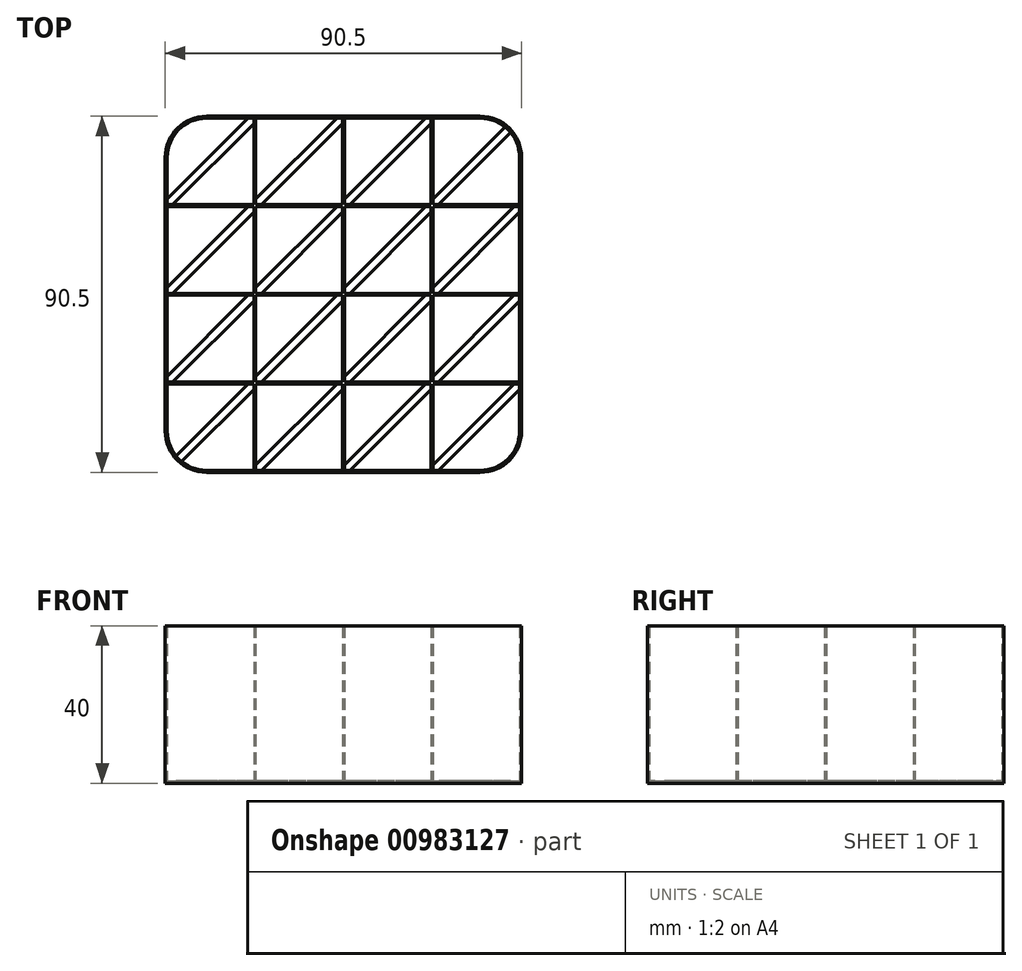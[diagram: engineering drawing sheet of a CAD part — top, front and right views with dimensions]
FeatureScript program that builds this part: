
annotation { "Feature Type Name" : "Feature", "Feature Type Description" : "" }
export const myFeature = defineFeature(function(context is Context, id is Id, definition is map)
    precondition{}
    {
        {
            assignVariable(context, id + "F0", {"name" : "wall", "anyValue" : 0.5});
        }
        {
            var Q0;
            Q0=qCreatedBy(makeId("Top.planeOp"),FACE);
            var sketch = newSketch(context, id + "F1", { "sketchPlane" : qUnion([Q0])});
            skLineSegment(sketch, "E0.bottom", {"start": v(0, 22) * mm, "end": v(22, 22) * mm});
            skLineSegment(sketch, "E0.top", {"start": v(0, 0) * mm, "end": v(22, 0) * mm});
            skLineSegment(sketch, "E0.left", {"start": v(0, 22) * mm, "end": v(0, 0) * mm});
            skLineSegment(sketch, "E0.right", {"start": v(22, 22) * mm, "end": v(22, 0) * mm});
            skLineSegment(sketch, "E1.0.1.0", {"start": v(22, 44.5) * mm, "end": v(22, 22.5) * mm});
            skLineSegment(sketch, "E1.0.1.1", {"start": v(0, 44.5) * mm, "end": v(22, 44.5) * mm});
            skLineSegment(sketch, "E1.0.1.2", {"start": v(0, 44.5) * mm, "end": v(0, 22.5) * mm});
            skLineSegment(sketch, "E1.0.1.3", {"start": v(0, 22.5) * mm, "end": v(22, 22.5) * mm});
            skLineSegment(sketch, "E1.0.2.0", {"start": v(22, 67) * mm, "end": v(22, 45) * mm});
            skLineSegment(sketch, "E1.0.2.1", {"start": v(0, 67) * mm, "end": v(22, 67) * mm});
            skLineSegment(sketch, "E1.0.2.2", {"start": v(0, 67) * mm, "end": v(0, 45) * mm});
            skLineSegment(sketch, "E1.0.2.3", {"start": v(0, 45) * mm, "end": v(22, 45) * mm});
            skLineSegment(sketch, "E1.0.3.0", {"start": v(22, 89.5) * mm, "end": v(22, 67.5) * mm});
            skLineSegment(sketch, "E1.0.3.1", {"start": v(0, 89.5) * mm, "end": v(22, 89.5) * mm});
            skLineSegment(sketch, "E1.0.3.2", {"start": v(0, 89.5) * mm, "end": v(0, 67.5) * mm});
            skLineSegment(sketch, "E1.0.3.3", {"start": v(0, 67.5) * mm, "end": v(22, 67.5) * mm});
            skLineSegment(sketch, "E1.1.0.0", {"start": v(44.5, 22) * mm, "end": v(44.5, 0) * mm});
            skLineSegment(sketch, "E1.1.0.1", {"start": v(22.5, 22) * mm, "end": v(44.5, 22) * mm});
            skLineSegment(sketch, "E1.1.0.2", {"start": v(22.5, 22) * mm, "end": v(22.5, 0) * mm});
            skLineSegment(sketch, "E1.1.0.3", {"start": v(22.5, 0) * mm, "end": v(44.5, 0) * mm});
            skLineSegment(sketch, "E1.1.1.0", {"start": v(44.5, 44.5) * mm, "end": v(44.5, 22.5) * mm});
            skLineSegment(sketch, "E1.1.1.1", {"start": v(22.5, 44.5) * mm, "end": v(44.5, 44.5) * mm});
            skLineSegment(sketch, "E1.1.1.2", {"start": v(22.5, 44.5) * mm, "end": v(22.5, 22.5) * mm});
            skLineSegment(sketch, "E1.1.1.3", {"start": v(22.5, 22.5) * mm, "end": v(44.5, 22.5) * mm});
            skLineSegment(sketch, "E1.1.2.0", {"start": v(44.5, 67) * mm, "end": v(44.5, 45) * mm});
            skLineSegment(sketch, "E1.1.2.1", {"start": v(22.5, 67) * mm, "end": v(44.5, 67) * mm});
            skLineSegment(sketch, "E1.1.2.2", {"start": v(22.5, 67) * mm, "end": v(22.5, 45) * mm});
            skLineSegment(sketch, "E1.1.2.3", {"start": v(22.5, 45) * mm, "end": v(44.5, 45) * mm});
            skLineSegment(sketch, "E1.1.3.0", {"start": v(44.5, 89.5) * mm, "end": v(44.5, 67.5) * mm});
            skLineSegment(sketch, "E1.1.3.1", {"start": v(22.5, 89.5) * mm, "end": v(44.5, 89.5) * mm});
            skLineSegment(sketch, "E1.1.3.2", {"start": v(22.5, 89.5) * mm, "end": v(22.5, 67.5) * mm});
            skLineSegment(sketch, "E1.1.3.3", {"start": v(22.5, 67.5) * mm, "end": v(44.5, 67.5) * mm});
            skLineSegment(sketch, "E1.2.0.0", {"start": v(67, 22) * mm, "end": v(67, 0) * mm});
            skLineSegment(sketch, "E1.2.0.1", {"start": v(45, 22) * mm, "end": v(67, 22) * mm});
            skLineSegment(sketch, "E1.2.0.2", {"start": v(45, 22) * mm, "end": v(45, 0) * mm});
            skLineSegment(sketch, "E1.2.0.3", {"start": v(45, 0) * mm, "end": v(67, 0) * mm});
            skLineSegment(sketch, "E1.2.1.0", {"start": v(67, 44.5) * mm, "end": v(67, 22.5) * mm});
            skLineSegment(sketch, "E1.2.1.1", {"start": v(45, 44.5) * mm, "end": v(67, 44.5) * mm});
            skLineSegment(sketch, "E1.2.1.2", {"start": v(45, 44.5) * mm, "end": v(45, 22.5) * mm});
            skLineSegment(sketch, "E1.2.1.3", {"start": v(45, 22.5) * mm, "end": v(67, 22.5) * mm});
            skLineSegment(sketch, "E1.2.2.0", {"start": v(67, 67) * mm, "end": v(67, 45) * mm});
            skLineSegment(sketch, "E1.2.2.1", {"start": v(45, 67) * mm, "end": v(67, 67) * mm});
            skLineSegment(sketch, "E1.2.2.2", {"start": v(45, 67) * mm, "end": v(45, 45) * mm});
            skLineSegment(sketch, "E1.2.2.3", {"start": v(45, 45) * mm, "end": v(67, 45) * mm});
            skLineSegment(sketch, "E1.2.3.0", {"start": v(67, 89.5) * mm, "end": v(67, 67.5) * mm});
            skLineSegment(sketch, "E1.2.3.1", {"start": v(45, 89.5) * mm, "end": v(67, 89.5) * mm});
            skLineSegment(sketch, "E1.2.3.2", {"start": v(45, 89.5) * mm, "end": v(45, 67.5) * mm});
            skLineSegment(sketch, "E1.2.3.3", {"start": v(45, 67.5) * mm, "end": v(67, 67.5) * mm});
            skLineSegment(sketch, "E1.3.0.0", {"start": v(89.5, 22) * mm, "end": v(89.5, 0) * mm});
            skLineSegment(sketch, "E1.3.0.1", {"start": v(67.5, 22) * mm, "end": v(89.5, 22) * mm});
            skLineSegment(sketch, "E1.3.0.2", {"start": v(67.5, 22) * mm, "end": v(67.5, 0) * mm});
            skLineSegment(sketch, "E1.3.0.3", {"start": v(67.5, 0) * mm, "end": v(89.5, 0) * mm});
            skLineSegment(sketch, "E1.3.1.0", {"start": v(89.5, 44.5) * mm, "end": v(89.5, 22.5) * mm});
            skLineSegment(sketch, "E1.3.1.1", {"start": v(67.5, 44.5) * mm, "end": v(89.5, 44.5) * mm});
            skLineSegment(sketch, "E1.3.1.2", {"start": v(67.5, 44.5) * mm, "end": v(67.5, 22.5) * mm});
            skLineSegment(sketch, "E1.3.1.3", {"start": v(67.5, 22.5) * mm, "end": v(89.5, 22.5) * mm});
            skLineSegment(sketch, "E1.3.2.0", {"start": v(89.5, 67) * mm, "end": v(89.5, 45) * mm});
            skLineSegment(sketch, "E1.3.2.1", {"start": v(67.5, 67) * mm, "end": v(89.5, 67) * mm});
            skLineSegment(sketch, "E1.3.2.2", {"start": v(67.5, 67) * mm, "end": v(67.5, 45) * mm});
            skLineSegment(sketch, "E1.3.2.3", {"start": v(67.5, 45) * mm, "end": v(89.5, 45) * mm});
            skLineSegment(sketch, "E1.3.3.0", {"start": v(89.5, 89.5) * mm, "end": v(89.5, 67.5) * mm});
            skLineSegment(sketch, "E1.3.3.1", {"start": v(67.5, 89.5) * mm, "end": v(89.5, 89.5) * mm});
            skLineSegment(sketch, "E1.3.3.2", {"start": v(67.5, 89.5) * mm, "end": v(67.5, 67.5) * mm});
            skLineSegment(sketch, "E1.3.3.3", {"start": v(67.5, 67.5) * mm, "end": v(89.5, 67.5) * mm});
            skLineSegment(sketch, "E1.direction1", {"start": v(22, 0) * mm, "end": v(44.5, 0) * mm, "construction": true});
            skLineSegment(sketch, "E1.direction2", {"start": v(22, 0) * mm, "end": v(22, 22.5) * mm, "construction": true});
            skLineSegment(sketch, "E2.bottom", {"start": v(-0.5, 90) * mm, "end": v(90, 90) * mm});
            skLineSegment(sketch, "E2.top", {"start": v(-0.5, -0.5) * mm, "end": v(90, -0.5) * mm});
            skLineSegment(sketch, "E2.left", {"start": v(-0.5, 90) * mm, "end": v(-0.5, -0.5) * mm});
            skLineSegment(sketch, "E2.right", {"start": v(90, 90) * mm, "end": v(90, -0.5) * mm});
            skSolve(sketch);
        }
        {
            var Q0;
            Q0=makeQuery(id+"F1.imprint","IMPRINT",FACE,{"disambiguationData":[TD([[makeQuery(id+"F1.imprint","IMPRINT",EDGE,{"derivedFrom":sQuery(id+"F1.wireOp",EDGE,"E0.bottom")}),1.0]])]});
            extrude(context, id + "F2", {"entities" : qUnion([Q0]), "depth" : 40 * mm, "offsetDistance" : 25 * mm});
        }
        {
            var Q0;
            Q0=makeQuery(id+"F2.opExtrude","CAP_FACE",FACE,{"disambiguationData":[OSD([sQuery(id+"F1.wireOp",EDGE,"E0.bottom"),sQuery(id+"F1.wireOp",EDGE,"E0.top"),sQuery(id+"F1.wireOp",EDGE,"E0.left"),sQuery(id+"F1.wireOp",EDGE,"E0.right"),sQuery(id+"F1.wireOp",EDGE,"E1.0.1.0"),sQuery(id+"F1.wireOp",EDGE,"E1.0.1.1"),sQuery(id+"F1.wireOp",EDGE,"E1.0.1.2"),sQuery(id+"F1.wireOp",EDGE,"E1.0.1.3"),sQuery(id+"F1.wireOp",EDGE,"E1.0.2.0"),sQuery(id+"F1.wireOp",EDGE,"E1.0.2.1"),sQuery(id+"F1.wireOp",EDGE,"E1.0.2.2"),sQuery(id+"F1.wireOp",EDGE,"E1.0.2.3"),sQuery(id+"F1.wireOp",EDGE,"E1.0.3.0"),sQuery(id+"F1.wireOp",EDGE,"E1.0.3.1"),sQuery(id+"F1.wireOp",EDGE,"E1.0.3.2"),sQuery(id+"F1.wireOp",EDGE,"E1.0.3.3"),sQuery(id+"F1.wireOp",EDGE,"E1.1.0.0"),sQuery(id+"F1.wireOp",EDGE,"E1.1.0.1"),sQuery(id+"F1.wireOp",EDGE,"E1.1.0.2"),sQuery(id+"F1.wireOp",EDGE,"E1.1.0.3"),sQuery(id+"F1.wireOp",EDGE,"E1.1.1.0"),sQuery(id+"F1.wireOp",EDGE,"E1.1.1.1"),sQuery(id+"F1.wireOp",EDGE,"E1.1.1.2"),sQuery(id+"F1.wireOp",EDGE,"E1.1.1.3"),sQuery(id+"F1.wireOp",EDGE,"E1.1.2.0"),sQuery(id+"F1.wireOp",EDGE,"E1.1.2.1"),sQuery(id+"F1.wireOp",EDGE,"E1.1.2.2"),sQuery(id+"F1.wireOp",EDGE,"E1.1.2.3"),sQuery(id+"F1.wireOp",EDGE,"E1.1.3.0"),sQuery(id+"F1.wireOp",EDGE,"E1.1.3.1"),sQuery(id+"F1.wireOp",EDGE,"E1.1.3.2"),sQuery(id+"F1.wireOp",EDGE,"E1.1.3.3"),sQuery(id+"F1.wireOp",EDGE,"E1.2.0.0"),sQuery(id+"F1.wireOp",EDGE,"E1.2.0.1"),sQuery(id+"F1.wireOp",EDGE,"E1.2.0.2"),sQuery(id+"F1.wireOp",EDGE,"E1.2.0.3"),sQuery(id+"F1.wireOp",EDGE,"E1.2.1.0"),sQuery(id+"F1.wireOp",EDGE,"E1.2.1.1"),sQuery(id+"F1.wireOp",EDGE,"E1.2.1.2"),sQuery(id+"F1.wireOp",EDGE,"E1.2.1.3"),sQuery(id+"F1.wireOp",EDGE,"E1.2.2.0"),sQuery(id+"F1.wireOp",EDGE,"E1.2.2.1"),sQuery(id+"F1.wireOp",EDGE,"E1.2.2.2"),sQuery(id+"F1.wireOp",EDGE,"E1.2.2.3"),sQuery(id+"F1.wireOp",EDGE,"E1.2.3.0"),sQuery(id+"F1.wireOp",EDGE,"E1.2.3.1"),sQuery(id+"F1.wireOp",EDGE,"E1.2.3.2"),sQuery(id+"F1.wireOp",EDGE,"E1.2.3.3"),sQuery(id+"F1.wireOp",EDGE,"E1.3.0.0"),sQuery(id+"F1.wireOp",EDGE,"E1.3.0.1"),sQuery(id+"F1.wireOp",EDGE,"E1.3.0.2"),sQuery(id+"F1.wireOp",EDGE,"E1.3.0.3"),sQuery(id+"F1.wireOp",EDGE,"E1.3.1.0"),sQuery(id+"F1.wireOp",EDGE,"E1.3.1.1"),sQuery(id+"F1.wireOp",EDGE,"E1.3.1.2"),sQuery(id+"F1.wireOp",EDGE,"E1.3.1.3"),sQuery(id+"F1.wireOp",EDGE,"E1.3.2.0"),sQuery(id+"F1.wireOp",EDGE,"E1.3.2.1"),sQuery(id+"F1.wireOp",EDGE,"E1.3.2.2"),sQuery(id+"F1.wireOp",EDGE,"E1.3.2.3"),sQuery(id+"F1.wireOp",EDGE,"E1.3.3.0"),sQuery(id+"F1.wireOp",EDGE,"E1.3.3.1"),sQuery(id+"F1.wireOp",EDGE,"E1.3.3.2"),sQuery(id+"F1.wireOp",EDGE,"E1.3.3.3"),sQuery(id+"F1.wireOp",EDGE,"E2.bottom"),sQuery(id+"F1.wireOp",EDGE,"E2.top"),sQuery(id+"F1.wireOp",EDGE,"E2.left"),sQuery(id+"F1.wireOp",EDGE,"E2.right")])],"isStart":true});
            var sketch = newSketch(context, id + "F3", { "sketchPlane" : qUnion([Q0])});
            skLineSegment(sketch, "E3", {"start": v(0, 0) * mm, "end": v(89.5, -89.5) * mm, "construction": true});
            skLineSegment(sketch, "E4", {"start": v(89.5, -88.09) * mm, "end": v(1.41, 0) * mm});
            skLineSegment(sketch, "E5", {"start": v(22.5, 0) * mm, "end": v(89.5, -67) * mm, "construction": true});
            skLineSegment(sketch, "E6", {"start": v(89.5, -44.5) * mm, "end": v(45, 0) * mm, "construction": true});
            skLineSegment(sketch, "E7.MirrorCS", {"start": v(88.09, -89.5) * mm, "end": v(0, -1.41) * mm});
            skLineSegment(sketch, "E8", {"start": v(23.91, 0) * mm, "end": v(89.5, -65.59) * mm});
            skLineSegment(sketch, "E9", {"start": v(22.5, -1.41) * mm, "end": v(88.09, -67) * mm});
            skLineSegment(sketch, "E10", {"start": v(46.41, 0) * mm, "end": v(89.5, -43.09) * mm});
            skLineSegment(sketch, "E11", {"start": v(88.09, -44.5) * mm, "end": v(45, -1.41) * mm});
            skLineSegment(sketch, "E12", {"start": v(67.5, 0) * mm, "end": v(89.5, -22) * mm, "construction": true});
            skLineSegment(sketch, "E13", {"start": v(68.91, 0) * mm, "end": v(89.5, -20.59) * mm});
            skLineSegment(sketch, "E14", {"start": v(88.09, -22) * mm, "end": v(67.5, -1.41) * mm});
            skLineSegment(sketch, "E15.MirrorCS", {"start": v(1.41, -22.5) * mm, "end": v(67, -88.09) * mm});
            skLineSegment(sketch, "E16.MirrorCS", {"start": v(0, -23.91) * mm, "end": v(65.59, -89.5) * mm});
            skLineSegment(sketch, "E17.MirrorCS", {"start": v(44.5, -88.09) * mm, "end": v(1.41, -45) * mm});
            skLineSegment(sketch, "E18.MirrorCS", {"start": v(0, -46.41) * mm, "end": v(43.09, -89.5) * mm});
            skLineSegment(sketch, "E19.MirrorCS", {"start": v(22, -88.09) * mm, "end": v(1.41, -67.5) * mm});
            skLineSegment(sketch, "E20.MirrorCS", {"start": v(0, -68.91) * mm, "end": v(20.59, -89.5) * mm});
            skSolve(sketch);
        }
        {
            var Q0;
            {var subQ4=sQuery(id+"F3.wireOp",EDGE,"E19.MirrorCS");Q0=makeQuery(id+"F3.imprint","IMPRINT",FACE,{"disambiguationData":[TD([[makeQuery(id+"F3.imprint","IMPRINT",EDGE,{"derivedFrom":subQ4}),1.0]])]});}
            var Q1;
            {var subQ5=sQuery(id+"F3.wireOp",EDGE,"E17.MirrorCS");var subQ6=makeQuery(id+"F2.opExtrude","CAP_EDGE",EDGE,{"disambiguationData":[OSD([sQuery(id+"F1.wireOp",EDGE,"E1.0.2.3")])],"isStart":true});var subQ7=makeQuery(id+"F3.imprint","INTERSECT",VERTEX,{"derivedFrom":[subQ6,subQ5]});Q1=makeQuery(id+"F3.imprint","IMPRINT",FACE,{"disambiguationData":[TD([[makeQuery(id+"F3.imprint","IMPRINT",EDGE,{"disambiguationData":[TD([[subQ7,1.0]])],"derivedFrom":subQ5}),1.0]])]});}
            var Q2;
            {var subQ1=makeQuery(id+"F2.opExtrude","CAP_EDGE",EDGE,{"disambiguationData":[OSD([sQuery(id+"F1.wireOp",EDGE,"E1.1.3.0")])],"isStart":true});var subQ5=sQuery(id+"F3.wireOp",EDGE,"E17.MirrorCS");var subQ6=makeQuery(id+"F3.imprint","INTERSECT",VERTEX,{"derivedFrom":[subQ1,subQ5]});Q2=makeQuery(id+"F3.imprint","IMPRINT",FACE,{"disambiguationData":[TD([[makeQuery(id+"F3.imprint","IMPRINT",EDGE,{"disambiguationData":[TD([[subQ6,-1.0]])],"derivedFrom":subQ5}),1.0]])]});}
            var Q3;
            {var subQ3=sQuery(id+"F3.wireOp",EDGE,"E15.MirrorCS");var subQ9=makeQuery(id+"F2.opExtrude","CAP_EDGE",EDGE,{"disambiguationData":[OSD([sQuery(id+"F1.wireOp",EDGE,"E1.0.1.3")])],"isStart":true});var subQ10=makeQuery(id+"F3.imprint","INTERSECT",VERTEX,{"derivedFrom":[subQ9,subQ3]});Q3=makeQuery(id+"F3.imprint","IMPRINT",FACE,{"disambiguationData":[TD([[makeQuery(id+"F3.imprint","IMPRINT",EDGE,{"disambiguationData":[TD([[subQ10,-1.0]])],"derivedFrom":subQ3}),-1.0]])]});}
            var Q4;
            {var subQ7=makeQuery(id+"F2.opExtrude","CAP_EDGE",EDGE,{"disambiguationData":[OSD([sQuery(id+"F1.wireOp",EDGE,"E1.1.2.3")])],"isStart":true});var subQ9=sQuery(id+"F3.wireOp",EDGE,"E15.MirrorCS");var subQ11=makeQuery(id+"F3.imprint","INTERSECT",VERTEX,{"derivedFrom":[subQ7,subQ9]});Q4=makeQuery(id+"F3.imprint","IMPRINT",FACE,{"disambiguationData":[TD([[makeQuery(id+"F3.imprint","IMPRINT",EDGE,{"disambiguationData":[TD([[subQ11,-1.0]])],"derivedFrom":subQ9}),-1.0]])]});}
            var Q5;
            {var subQ1=makeQuery(id+"F2.opExtrude","CAP_EDGE",EDGE,{"disambiguationData":[OSD([sQuery(id+"F1.wireOp",EDGE,"E1.2.3.0")])],"isStart":true});var subQ3=sQuery(id+"F3.wireOp",EDGE,"E15.MirrorCS");var subQ4=makeQuery(id+"F3.imprint","INTERSECT",VERTEX,{"derivedFrom":[subQ1,subQ3]});Q5=makeQuery(id+"F3.imprint","IMPRINT",FACE,{"disambiguationData":[TD([[makeQuery(id+"F3.imprint","IMPRINT",EDGE,{"disambiguationData":[TD([[subQ4,1.0]])],"derivedFrom":subQ3}),-1.0]])]});}
            var Q6;
            {var subQ1=makeQuery(id+"F2.opExtrude","CAP_EDGE",EDGE,{"disambiguationData":[OSD([sQuery(id+"F1.wireOp",EDGE,"E1.3.3.0")])],"isStart":true});var subQ3=sQuery(id+"F3.wireOp",EDGE,"E4");var subQ4=makeQuery(id+"F3.imprint","INTERSECT",VERTEX,{"derivedFrom":[subQ1,subQ3]});Q6=makeQuery(id+"F3.imprint","IMPRINT",FACE,{"disambiguationData":[TD([[makeQuery(id+"F3.imprint","IMPRINT",EDGE,{"disambiguationData":[TD([[subQ4,-1.0]])],"derivedFrom":subQ3}),1.0]])]});}
            var Q7;
            {var subQ1=makeQuery(id+"F2.opExtrude","CAP_EDGE",EDGE,{"disambiguationData":[OSD([sQuery(id+"F1.wireOp",EDGE,"E1.2.2.0")])],"isStart":true});var subQ9=sQuery(id+"F3.wireOp",EDGE,"E4");var subQ11=makeQuery(id+"F3.imprint","INTERSECT",VERTEX,{"derivedFrom":[subQ1,subQ9]});Q7=makeQuery(id+"F3.imprint","IMPRINT",FACE,{"disambiguationData":[TD([[makeQuery(id+"F3.imprint","IMPRINT",EDGE,{"disambiguationData":[TD([[subQ11,-1.0]])],"derivedFrom":subQ9}),1.0]])]});}
            var Q8;
            {var subQ1=makeQuery(id+"F2.opExtrude","CAP_EDGE",EDGE,{"disambiguationData":[OSD([sQuery(id+"F1.wireOp",EDGE,"E1.1.1.0")])],"isStart":true});var subQ7=sQuery(id+"F3.wireOp",EDGE,"E4");var subQ8=makeQuery(id+"F3.imprint","INTERSECT",VERTEX,{"derivedFrom":[subQ1,subQ7]});Q8=makeQuery(id+"F3.imprint","IMPRINT",FACE,{"disambiguationData":[TD([[makeQuery(id+"F3.imprint","IMPRINT",EDGE,{"disambiguationData":[TD([[subQ8,-1.0]])],"derivedFrom":subQ7}),1.0]])]});}
            var Q9;
            {var subQ7=makeQuery(id+"F2.opExtrude","CAP_EDGE",EDGE,{"disambiguationData":[OSD([sQuery(id+"F1.wireOp",EDGE,"E0.top")])],"isStart":true});var subQ9=sQuery(id+"F3.wireOp",EDGE,"E4");var subQ10=makeQuery(id+"F3.imprint","INTERSECT",VERTEX,{"derivedFrom":[subQ7,subQ9]});Q9=makeQuery(id+"F3.imprint","IMPRINT",FACE,{"disambiguationData":[TD([[makeQuery(id+"F3.imprint","IMPRINT",EDGE,{"disambiguationData":[TD([[subQ10,1.0]])],"derivedFrom":subQ9}),1.0]])]});}
            var Q10;
            {var subQ3=sQuery(id+"F3.wireOp",EDGE,"E8");var subQ9=makeQuery(id+"F2.opExtrude","CAP_EDGE",EDGE,{"disambiguationData":[OSD([sQuery(id+"F1.wireOp",EDGE,"E1.1.0.3")])],"isStart":true});var subQ10=makeQuery(id+"F3.imprint","INTERSECT",VERTEX,{"derivedFrom":[subQ9,subQ3]});Q10=makeQuery(id+"F3.imprint","IMPRINT",FACE,{"disambiguationData":[TD([[makeQuery(id+"F3.imprint","IMPRINT",EDGE,{"disambiguationData":[TD([[subQ10,-1.0]])],"derivedFrom":subQ3}),-1.0]])]});}
            var Q11;
            {var subQ3=sQuery(id+"F3.wireOp",EDGE,"E8");var subQ9=makeQuery(id+"F2.opExtrude","CAP_EDGE",EDGE,{"disambiguationData":[OSD([sQuery(id+"F1.wireOp",EDGE,"E1.2.1.3")])],"isStart":true});var subQ10=makeQuery(id+"F3.imprint","INTERSECT",VERTEX,{"derivedFrom":[subQ9,subQ3]});Q11=makeQuery(id+"F3.imprint","IMPRINT",FACE,{"disambiguationData":[TD([[makeQuery(id+"F3.imprint","IMPRINT",EDGE,{"disambiguationData":[TD([[subQ10,-1.0]])],"derivedFrom":subQ3}),-1.0]])]});}
            var Q12;
            {var subQ1=makeQuery(id+"F2.opExtrude","CAP_EDGE",EDGE,{"disambiguationData":[OSD([sQuery(id+"F1.wireOp",EDGE,"E1.3.2.0")])],"isStart":true});var subQ3=sQuery(id+"F3.wireOp",EDGE,"E8");var subQ4=makeQuery(id+"F3.imprint","INTERSECT",VERTEX,{"derivedFrom":[subQ1,subQ3]});Q12=makeQuery(id+"F3.imprint","IMPRINT",FACE,{"disambiguationData":[TD([[makeQuery(id+"F3.imprint","IMPRINT",EDGE,{"disambiguationData":[TD([[subQ4,1.0]])],"derivedFrom":subQ3}),-1.0]])]});}
            var Q13;
            {var subQ1=makeQuery(id+"F2.opExtrude","CAP_EDGE",EDGE,{"disambiguationData":[OSD([sQuery(id+"F1.wireOp",EDGE,"E1.3.1.0")])],"isStart":true});var subQ3=sQuery(id+"F3.wireOp",EDGE,"E10");var subQ4=makeQuery(id+"F3.imprint","INTERSECT",VERTEX,{"derivedFrom":[subQ1,subQ3]});Q13=makeQuery(id+"F3.imprint","IMPRINT",FACE,{"disambiguationData":[TD([[makeQuery(id+"F3.imprint","IMPRINT",EDGE,{"disambiguationData":[TD([[subQ4,1.0]])],"derivedFrom":subQ3}),-1.0]])]});}
            var Q14;
            {var subQ3=sQuery(id+"F3.wireOp",EDGE,"E10");var subQ9=makeQuery(id+"F2.opExtrude","CAP_EDGE",EDGE,{"disambiguationData":[OSD([sQuery(id+"F1.wireOp",EDGE,"E1.2.0.3")])],"isStart":true});var subQ10=makeQuery(id+"F3.imprint","INTERSECT",VERTEX,{"derivedFrom":[subQ9,subQ3]});Q14=makeQuery(id+"F3.imprint","IMPRINT",FACE,{"disambiguationData":[TD([[makeQuery(id+"F3.imprint","IMPRINT",EDGE,{"disambiguationData":[TD([[subQ10,-1.0]])],"derivedFrom":subQ3}),-1.0]])]});}
            var Q15;
            {var subQ4=sQuery(id+"F3.wireOp",EDGE,"E13");Q15=makeQuery(id+"F3.imprint","IMPRINT",FACE,{"disambiguationData":[TD([[makeQuery(id+"F3.imprint","IMPRINT",EDGE,{"derivedFrom":subQ4}),-1.0]])]});}
            extrude(context, id + "F4", {"entities" : qUnion([Q0, Q1, Q2, Q3, Q4, Q5, Q6, Q7, Q8, Q9, Q10, Q11, Q12, Q13, Q14, Q15]), "operationType" : NewBodyOperationType.ADD, "oppositeDirection" : true, "depth" : 0.6 * mm, "offsetDistance" : 25 * mm});
        }
        {
            var Q0;
            Q0=makeQuery(id+"F2.opExtrude","SWEPT_EDGE",EDGE,{"disambiguationData":[OSD([sQuery(id+"F1.wireOp",EDGE,"E1.3.0.0"),sQuery(id+"F1.wireOp",EDGE,"E1.3.0.3")])]});
            var Q1;
            Q1=makeQuery(id+"F2.opExtrude","SWEPT_EDGE",EDGE,{"disambiguationData":[OSD([sQuery(id+"F1.wireOp",EDGE,"E0.top"),sQuery(id+"F1.wireOp",EDGE,"E0.left")])]});
            var Q2;
            Q2=makeQuery(id+"F2.opExtrude","SWEPT_EDGE",EDGE,{"disambiguationData":[OSD([sQuery(id+"F1.wireOp",EDGE,"E1.0.3.1"),sQuery(id+"F1.wireOp",EDGE,"E1.0.3.2")])]});
            var Q3;
            Q3=makeQuery(id+"F2.opExtrude","SWEPT_EDGE",EDGE,{"disambiguationData":[OSD([sQuery(id+"F1.wireOp",EDGE,"E1.3.3.0"),sQuery(id+"F1.wireOp",EDGE,"E1.3.3.1")])]});
            fillet(context, id + "F5", {"entities" : qUnion([Q0, Q1, Q2, Q3]), "radius" : 10 * mm, "tangentPropagation" : true, "allowEdgeOverflow" : false});
        }
        {
            var Q0;
            Q0=makeQuery(id+"F2.opExtrude","SWEPT_EDGE",EDGE,{"disambiguationData":[OSD([sQuery(id+"F1.wireOp",EDGE,"E2.top"),sQuery(id+"F1.wireOp",EDGE,"E2.right")])]});
            var Q1;
            Q1=makeQuery(id+"F2.opExtrude","SWEPT_EDGE",EDGE,{"disambiguationData":[OSD([sQuery(id+"F1.wireOp",EDGE,"E2.top"),sQuery(id+"F1.wireOp",EDGE,"E2.left")])]});
            var Q2;
            Q2=makeQuery(id+"F2.opExtrude","SWEPT_EDGE",EDGE,{"disambiguationData":[OSD([sQuery(id+"F1.wireOp",EDGE,"E2.bottom"),sQuery(id+"F1.wireOp",EDGE,"E2.left")])]});
            var Q3;
            Q3=makeQuery(id+"F2.opExtrude","SWEPT_EDGE",EDGE,{"disambiguationData":[OSD([sQuery(id+"F1.wireOp",EDGE,"E2.bottom"),sQuery(id+"F1.wireOp",EDGE,"E2.right")])]});
            fillet(context, id + "F6", {"entities" : qUnion([Q0, Q1, Q2, Q3]), "radius" : (10 + getVariable(context, 'wall')) * mm, "tangentPropagation" : true, "allowEdgeOverflow" : false});
        }
    });
